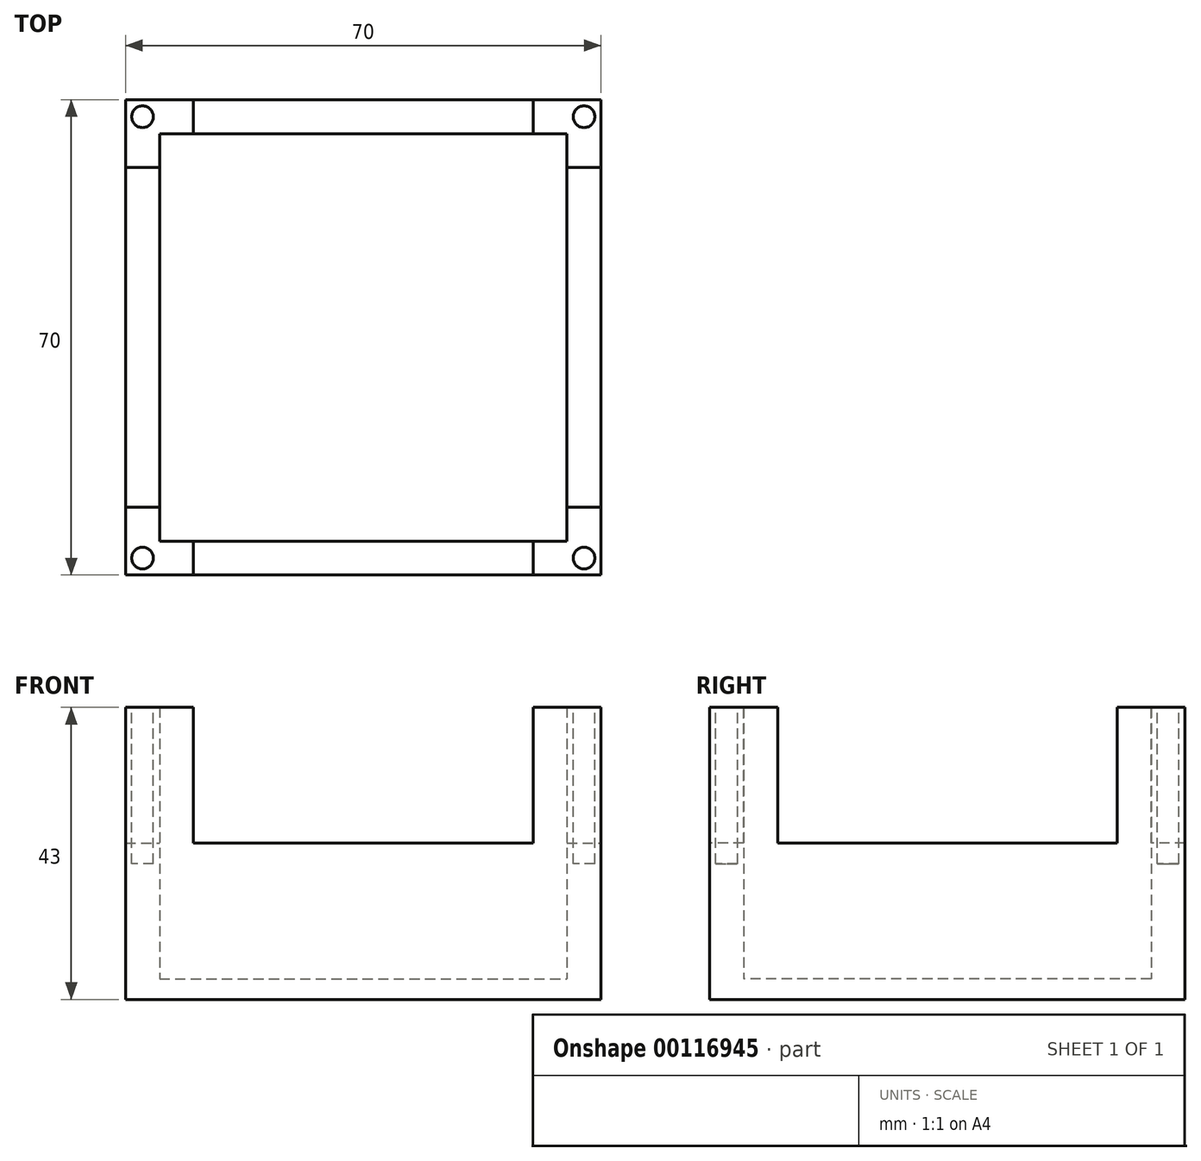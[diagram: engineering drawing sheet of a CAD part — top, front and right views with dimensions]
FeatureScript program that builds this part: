
annotation { "Feature Type Name" : "Feature", "Feature Type Description" : "" }
export const myFeature = defineFeature(function(context is Context, id is Id, definition is map)
    precondition{}
    {
        {
            var Q0;
            Q0=qCreatedBy(makeId("Top.planeOp"),FACE);
            var sketch = newSketch(context, id + "F0", { "sketchPlane" : qUnion([Q0])});
            skLineSegment(sketch, "E0.bottom", {"start": v(-30, 30) * mm, "end": v(30, 30) * mm});
            skLineSegment(sketch, "E0.top", {"start": v(-30, -30) * mm, "end": v(30, -30) * mm});
            skLineSegment(sketch, "E0.left", {"start": v(-30, 30) * mm, "end": v(-30, -30) * mm});
            skLineSegment(sketch, "E0.right", {"start": v(30, 30) * mm, "end": v(30, -30) * mm});
            skPoint(sketch, "E0.middle", {"position": v(0, 0) * mm});
            skLineSegment(sketch, "E1.0", {"start": v(-35, 35) * mm, "end": v(35, 35) * mm});
            skLineSegment(sketch, "E1.1", {"start": v(-35, 35) * mm, "end": v(-35, -35) * mm});
            skLineSegment(sketch, "E1.2", {"start": v(-35, -35) * mm, "end": v(35, -35) * mm});
            skLineSegment(sketch, "E1.3", {"start": v(35, 35) * mm, "end": v(35, -35) * mm});
            skSolve(sketch);
        }
        {
            var Q0;
            Q0 = qSketchRegion(id + "F0", true);
            var Q1;
            Q1=makeQuery(id+"F0.imprint","IMPRINT",FACE,{"disambiguationData":[TD([[makeQuery(id+"F0.imprint","IMPRINT",EDGE,{"derivedFrom":sQuery(id+"F0.wireOp",EDGE,"E0.bottom")}),-1.0]])]});
            extrude(context, id + "F1", {"entities" : qUnion([Q0, Q1]), "depth" : 3 * mm});
        }
        {
            var Q0;
            Q0=makeQuery(id+"F1.opExtrude","CAP_FACE",FACE,{"disambiguationData":[OSD([sQuery(id+"F0.wireOp",EDGE,"E1.0"),sQuery(id+"F0.wireOp",EDGE,"E1.1"),sQuery(id+"F0.wireOp",EDGE,"E1.2"),sQuery(id+"F0.wireOp",EDGE,"E1.3")])],"isStart":false});
            var sketch = newSketch(context, id + "F2", { "sketchPlane" : qUnion([Q0])});
            skLineSegment(sketch, "E2.0", {"start": v(-30, 30) * mm, "end": v(30, 30) * mm});
            skLineSegment(sketch, "E2.1", {"start": v(-30, -30) * mm, "end": v(30, -30) * mm});
            skLineSegment(sketch, "E2.2", {"start": v(-30, 30) * mm, "end": v(-30, -30) * mm});
            skLineSegment(sketch, "E2.3", {"start": v(30, 30) * mm, "end": v(30, -30) * mm});
            skPoint(sketch, "E2.4", {"position": v(0, 0) * mm});
            skLineSegment(sketch, "E2.5", {"start": v(-35, 35) * mm, "end": v(35, 35) * mm});
            skLineSegment(sketch, "E2.6", {"start": v(-35, 35) * mm, "end": v(-35, -35) * mm});
            skLineSegment(sketch, "E2.7", {"start": v(-35, -35) * mm, "end": v(35, -35) * mm});
            skLineSegment(sketch, "E2.8", {"start": v(35, 35) * mm, "end": v(35, -35) * mm});
            skSolve(sketch);
        }
        {
            var Q0;
            Q0=makeQuery(id+"F2.imprint","IMPRINT",FACE,{"disambiguationData":[TD([[makeQuery(id+"F2.imprint","IMPRINT",EDGE,{"derivedFrom":sQuery(id+"F2.wireOp",EDGE,"E2.0")}),1.0]])]});
            extrude(context, id + "F3", {"entities" : qUnion([Q0]), "operationType" : NewBodyOperationType.ADD, "depth" : 40 * mm});
        }
        {
            var Q0;
            Q0=makeQuery(id+"F3.boolean.opBoolean","MERGE",FACE,{"derivedFrom":[makeQuery(id+"F1.opExtrude","SWEPT_FACE",FACE,{"disambiguationData":[OSD([sQuery(id+"F0.wireOp",EDGE,"E1.2")])]}),makeQuery(id+"F3.opExtrude","SWEPT_FACE",FACE,{"disambiguationData":[OSD([sQuery(id+"F2.wireOp",EDGE,"E2.7")])]})]});
            var sketch = newSketch(context, id + "F4", { "sketchPlane" : qUnion([Q0])});
            skLineSegment(sketch, "E3", {"start": v(0, 43) * mm, "end": v(0, 0) * mm, "construction": true});
            skLineSegment(sketch, "E4.bottom", {"start": v(-25, 43) * mm, "end": v(25, 43) * mm});
            skLineSegment(sketch, "E4.top", {"start": v(-25, 23) * mm, "end": v(25, 23) * mm});
            skLineSegment(sketch, "E4.left", {"start": v(-25, 43) * mm, "end": v(-25, 23) * mm});
            skLineSegment(sketch, "E4.right", {"start": v(25, 43) * mm, "end": v(25, 23) * mm});
            skPoint(sketch, "E4.middle", {"position": v(0, 33) * mm});
            skSolve(sketch);
        }
        {
            var Q0;
            Q0 = qSketchRegion(id + "F4", true);
            extrude(context, id + "F5", {"entities" : qUnion([Q0]), "operationType" : NewBodyOperationType.REMOVE, "oppositeDirection" : true, "depth" : 71 * mm});
        }
        {
            var Q0;
            Q0=makeQuery(id+"F3.boolean.opBoolean","MERGE",FACE,{"derivedFrom":[makeQuery(id+"F1.opExtrude","SWEPT_FACE",FACE,{"disambiguationData":[OSD([sQuery(id+"F0.wireOp",EDGE,"E1.3")])]}),makeQuery(id+"F3.opExtrude","SWEPT_FACE",FACE,{"disambiguationData":[OSD([sQuery(id+"F2.wireOp",EDGE,"E2.8")])]})]});
            var sketch = newSketch(context, id + "F6", { "sketchPlane" : qUnion([Q0])});
            skLineSegment(sketch, "E5", {"start": v(0, 43) * mm, "end": v(0, 0) * mm, "construction": true});
            skLineSegment(sketch, "E6.bottom", {"start": v(-25, 43) * mm, "end": v(25, 43) * mm});
            skLineSegment(sketch, "E6.top", {"start": v(-25, 23) * mm, "end": v(25, 23) * mm});
            skLineSegment(sketch, "E6.left", {"start": v(-25, 43) * mm, "end": v(-25, 23) * mm});
            skLineSegment(sketch, "E6.right", {"start": v(25, 43) * mm, "end": v(25, 23) * mm});
            skPoint(sketch, "E6.middle", {"position": v(0, 33) * mm});
            skSolve(sketch);
        }
        {
            var Q0;
            Q0 = qSketchRegion(id + "F6", true);
            extrude(context, id + "F7", {"entities" : qUnion([Q0]), "operationType" : NewBodyOperationType.REMOVE, "oppositeDirection" : true, "depth" : 70 * mm});
        }
        {
            var Q0;
            Q0=makeQuery(id+"F0.imprint","IMPRINT",FACE,{"disambiguationData":[TD([[makeQuery(id+"F0.imprint","IMPRINT",EDGE,{"derivedFrom":sQuery(id+"F0.wireOp",EDGE,"E0.bottom")}),1.0]])]});
            var sketch = newSketch(context, id + "F8", { "sketchPlane" : qUnion([Q0])});
            skSolve(sketch);
        }
        {
            var Q0;
            Q0=makeQuery(id+"F8.imprint","IMPRINT",FACE,{"disambiguationData":[TD([[makeQuery(id+"F8.imprint","IMPRINT",EDGE,{"derivedFrom":makeQuery(id+"F0.imprint","IMPRINT",EDGE,{"derivedFrom":sQuery(id+"F0.wireOp",EDGE,"E0.bottom")})}),1.0]])]});
            var sketch = newSketch(context, id + "F9", { "sketchPlane" : qUnion([Q0])});
            skLineSegment(sketch, "E7.0", {"start": v(-30, 30) * mm, "end": v(30, 30) * mm});
            skLineSegment(sketch, "E7.1", {"start": v(-30, -30) * mm, "end": v(30, -30) * mm});
            skLineSegment(sketch, "E7.2", {"start": v(-30, 30) * mm, "end": v(-30, -30) * mm});
            skLineSegment(sketch, "E7.3", {"start": v(30, 30) * mm, "end": v(30, -30) * mm});
            skLineSegment(sketch, "E7.4", {"start": v(-35, 35) * mm, "end": v(35, 35) * mm});
            skLineSegment(sketch, "E7.5", {"start": v(-35, 35) * mm, "end": v(-35, -35) * mm});
            skLineSegment(sketch, "E7.6", {"start": v(-35, -35) * mm, "end": v(35, -35) * mm});
            skLineSegment(sketch, "E7.7", {"start": v(35, 35) * mm, "end": v(35, -35) * mm});
            skLineSegment(sketch, "E7.8", {"start": v(-25, -35) * mm, "end": v(25, -35) * mm});
            skLineSegment(sketch, "E7.9", {"start": v(-25, -35) * mm, "end": v(25, -35) * mm});
            skLineSegment(sketch, "E7.10", {"start": v(-35, 35) * mm, "end": v(35, 35) * mm});
            skLineSegment(sketch, "E7.11", {"start": v(-35, 35) * mm, "end": v(-35, -35) * mm});
            skLineSegment(sketch, "E7.12", {"start": v(-35, -35) * mm, "end": v(35, -35) * mm});
            skLineSegment(sketch, "E7.13", {"start": v(35, 35) * mm, "end": v(35, -35) * mm});
            skLineSegment(sketch, "E7.15", {"start": v(35, -25) * mm, "end": v(35, -35) * mm});
            skLineSegment(sketch, "E7.16", {"start": v(35, -25) * mm, "end": v(35, 25) * mm});
            skLineSegment(sketch, "E7.17", {"start": v(-35, -25) * mm, "end": v(-35, 25) * mm});
            skLineSegment(sketch, "E7.18", {"start": v(-25, 35) * mm, "end": v(-25, 30) * mm});
            skLineSegment(sketch, "E7.19", {"start": v(-35, 35) * mm, "end": v(-35, 25) * mm});
            skLineSegment(sketch, "E7.20", {"start": v(-35, -25) * mm, "end": v(-35, -35) * mm});
            skLineSegment(sketch, "E7.21", {"start": v(35, 35) * mm, "end": v(35, 25) * mm});
            skLineSegment(sketch, "E7.22", {"start": v(-35, -25) * mm, "end": v(-30, -25) * mm});
            skLineSegment(sketch, "E7.25", {"start": v(-30, 30) * mm, "end": v(-30, -30) * mm});
            skLineSegment(sketch, "E7.26", {"start": v(30, 30) * mm, "end": v(30, -30) * mm});
            skLineSegment(sketch, "E7.27", {"start": v(-25, -30) * mm, "end": v(-25, -35) * mm});
            skLineSegment(sketch, "E7.28", {"start": v(-35, 35) * mm, "end": v(-25, 35) * mm});
            skLineSegment(sketch, "E7.29", {"start": v(25, 35) * mm, "end": v(35, 35) * mm});
            skLineSegment(sketch, "E7.36", {"start": v(-30, 30) * mm, "end": v(-30, 25) * mm});
            skLineSegment(sketch, "E7.37", {"start": v(-30, -25) * mm, "end": v(-30, -30) * mm});
            skLineSegment(sketch, "E7.38", {"start": v(30, -25) * mm, "end": v(30, 25) * mm});
            skLineSegment(sketch, "E7.39", {"start": v(30, 30) * mm, "end": v(30, 25) * mm});
            skLineSegment(sketch, "E7.40", {"start": v(30, -25) * mm, "end": v(30, -30) * mm});
            skLineSegment(sketch, "E7.41", {"start": v(-30, -25) * mm, "end": v(-30, 25) * mm});
            skLineSegment(sketch, "E7.42", {"start": v(25, -30) * mm, "end": v(25, -35) * mm});
            skLineSegment(sketch, "E7.45", {"start": v(-30, 30) * mm, "end": v(30, 30) * mm});
            skLineSegment(sketch, "E7.46", {"start": v(-30, -30) * mm, "end": v(30, -30) * mm});
            skLineSegment(sketch, "E7.47", {"start": v(25, 35) * mm, "end": v(-25, 35) * mm});
            skLineSegment(sketch, "E7.48", {"start": v(30, 25) * mm, "end": v(35, 25) * mm});
            skLineSegment(sketch, "E7.49", {"start": v(25, 35) * mm, "end": v(25, 30) * mm});
            skLineSegment(sketch, "E7.50", {"start": v(-25, -35) * mm, "end": v(25, -35) * mm});
            skLineSegment(sketch, "E7.51", {"start": v(-35, -25) * mm, "end": v(-30, -25) * mm});
            skLineSegment(sketch, "E7.52", {"start": v(-35, -35) * mm, "end": v(-25, -35) * mm});
            skLineSegment(sketch, "E7.53", {"start": v(25, -35) * mm, "end": v(35, -35) * mm});
            skLineSegment(sketch, "E7.54", {"start": v(-35, 25) * mm, "end": v(-30, 25) * mm});
            skLineSegment(sketch, "E7.55", {"start": v(30, 25) * mm, "end": v(35, 25) * mm});
            skLineSegment(sketch, "E7.56", {"start": v(-35, 25) * mm, "end": v(-30, 25) * mm});
            skLineSegment(sketch, "E7.58", {"start": v(30, -25) * mm, "end": v(35, -25) * mm});
            skLineSegment(sketch, "E7.69", {"start": v(25, -30) * mm, "end": v(-25, -30) * mm});
            skLineSegment(sketch, "E7.71", {"start": v(25, -30) * mm, "end": v(25, -35) * mm});
            skLineSegment(sketch, "E7.72", {"start": v(25, 35) * mm, "end": v(25, 30) * mm});
            skLineSegment(sketch, "E7.73", {"start": v(-30, 30) * mm, "end": v(-25, 30) * mm});
            skLineSegment(sketch, "E7.74", {"start": v(25, 30) * mm, "end": v(30, 30) * mm});
            skLineSegment(sketch, "E7.75", {"start": v(-30, -30) * mm, "end": v(-25, -30) * mm});
            skLineSegment(sketch, "E7.77", {"start": v(25, -30) * mm, "end": v(30, -30) * mm});
            skLineSegment(sketch, "E7.78", {"start": v(-25, -30) * mm, "end": v(-25, -35) * mm});
            skLineSegment(sketch, "E7.79", {"start": v(-25, 35) * mm, "end": v(-25, 30) * mm});
            skLineSegment(sketch, "E7.80", {"start": v(25, 30) * mm, "end": v(-25, 30) * mm});
            skLineSegment(sketch, "E7.82", {"start": v(30, -25) * mm, "end": v(35, -25) * mm});
            skSolve(sketch);
        }
        {
            var Q0;
            Q0=qCreatedBy(makeId("Top.planeOp"),FACE);
            cPlane(context, id + "F10", {"entities" : qUnion([Q0]), "cplaneType" : CPlaneType.OFFSET, "offset" : 45 * mm, "width" : 150 * mm, "height" : 150 * mm});
        }
        {
            var Q0;
            Q0=qCreatedBy(id+"F10.planeOp",FACE);
            var sketch = newSketch(context, id + "F11", { "sketchPlane" : qUnion([Q0])});
            skPoint(sketch, "E8.0", {"position": v(35, 35) * mm});
            skPoint(sketch, "E9.0", {"position": v(30, 30) * mm});
            skPoint(sketch, "E10.0", {"position": v(30, -30) * mm});
            skPoint(sketch, "E11.0", {"position": v(35, -35) * mm});
            skPoint(sketch, "E12.0", {"position": v(-30, -30) * mm});
            skPoint(sketch, "E13.0", {"position": v(-35, -35) * mm});
            skPoint(sketch, "E14.0", {"position": v(-30, 30) * mm});
            skPoint(sketch, "E15.0", {"position": v(-35, 35) * mm});
            skLineSegment(sketch, "E16", {"start": v(30, 30) * mm, "end": v(35, 35) * mm, "construction": true});
            skLineSegment(sketch, "E17", {"start": v(30, -30) * mm, "end": v(35, -35) * mm, "construction": true});
            skLineSegment(sketch, "E18", {"start": v(-30, -30) * mm, "end": v(-35, -35) * mm, "construction": true});
            skLineSegment(sketch, "E19", {"start": v(-30, 30) * mm, "end": v(-35, 35) * mm, "construction": true});
            skCircle(sketch, "E20", {"center": v(32.5, 32.5) * mm, "radius": 1.6 * mm});
            skLineSegment(sketch, "E21", {"start": v(-51.1, 0) * mm, "end": v(47.52, 0) * mm, "construction": true});
            skLineSegment(sketch, "E22", {"start": v(0, -59.96) * mm, "end": v(0, 59.56) * mm, "construction": true});
            skCircle(sketch, "E23.MirrorC", {"center": v(32.5, -32.5) * mm, "radius": 1.6 * mm});
            skCircle(sketch, "E24.MirrorC", {"center": v(-32.5, 32.5) * mm, "radius": 1.6 * mm});
            skCircle(sketch, "E25.MirrorC", {"center": v(-32.5, -32.5) * mm, "radius": 1.6 * mm});
            skSolve(sketch);
        }
        {
            var Q0;
            Q0 = qSketchRegion(id + "F11", true);
            var Q1;
            Q1 = qConstructionFilter(qBodyType(qCreatedBy(id + "F11" ,EDGE), BodyType.WIRE), ConstructionObject.NO);
            extrude(context, id + "F12", {"entities" : qUnion([Q0]), "operationType" : NewBodyOperationType.REMOVE, "surfaceEntities" : qUnion([Q1]), "oppositeDirection" : true, "depth" : 25 * mm});
        }
    });
